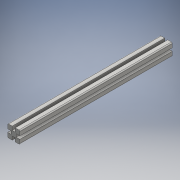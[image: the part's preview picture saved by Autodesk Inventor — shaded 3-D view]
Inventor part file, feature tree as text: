
AUTODESK INVENTOR PART (.ipt)
format: ipt  version: 2016 (Build 200138000, 138)  size: 120,832 bytes
history: native  units: mm
features: extrude x1, sketch x1
ambient origin geometry x8: Origin, YZ Plane, XZ Plane, XY Plane, X Axis, Y Axis, Z Axis, Center Point
bodies: Solid1 (feature_tree)
feature tree (2):
  extrude  "Extrusion1"  [1 undecoded]
  sketch  "Sketch1"  dims[d0=500.0mm d1=0.0mm]
note: 1 required parameter value undecoded (feature->parameter linkage not recoverable at this tier; creation-order binding heuristic only, values carry confidence <= 0.55)
